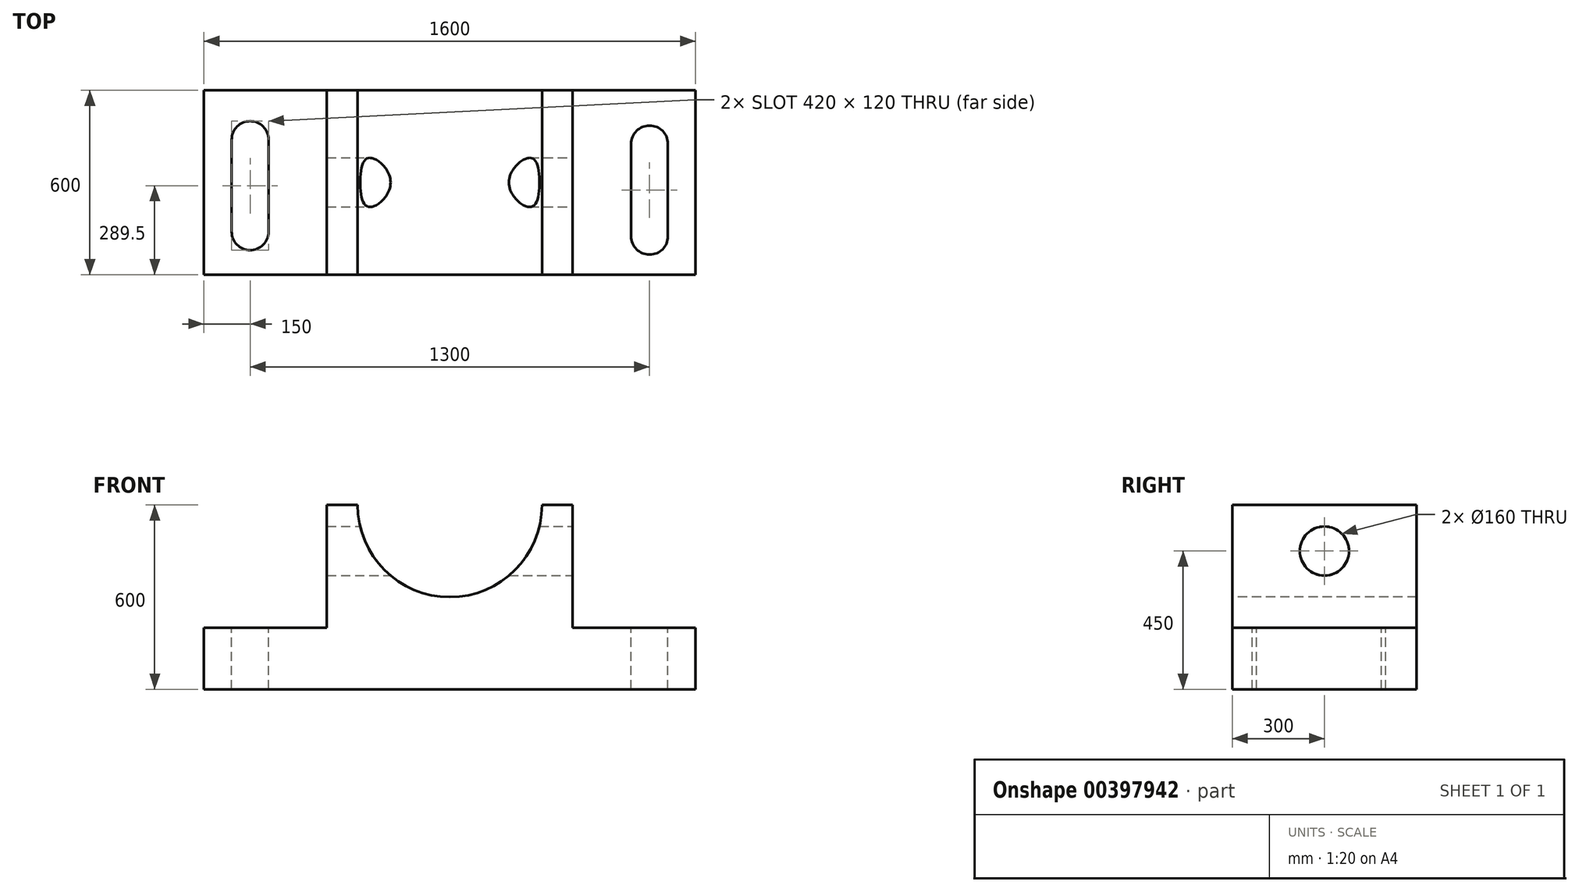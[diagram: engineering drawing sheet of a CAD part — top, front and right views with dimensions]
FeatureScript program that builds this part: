
annotation { "Feature Type Name" : "Feature", "Feature Type Description" : "" }
export const myFeature = defineFeature(function(context is Context, id is Id, definition is map)
    precondition{}
    {
        {
            var Q0;
            Q0=qCreatedBy(makeId("Front.planeOp"),FACE);
            var sketch = newSketch(context, id + "F0", { "sketchPlane" : qUnion([Q0])});
            skLineSegment(sketch, "E0.bottom", {"start": v(-800, -300) * mm, "end": v(800, -300) * mm});
            skLineSegment(sketch, "E0.top", {"start": v(-800, 300) * mm, "end": v(800, 300) * mm});
            skLineSegment(sketch, "E0.left", {"start": v(-800, -300) * mm, "end": v(-800, 300) * mm});
            skLineSegment(sketch, "E0.right", {"start": v(800, -300) * mm, "end": v(800, 300) * mm});
            skPoint(sketch, "E0.middle", {"position": v(0, 0) * mm});
            skLineSegment(sketch, "E1.bottom", {"start": v(-400, 300) * mm, "end": v(-800, 300) * mm});
            skLineSegment(sketch, "E1.top", {"start": v(-400, -100) * mm, "end": v(-800, -100) * mm});
            skLineSegment(sketch, "E1.left", {"start": v(-400, 300) * mm, "end": v(-400, -100) * mm});
            skLineSegment(sketch, "E1.right", {"start": v(-800, 300) * mm, "end": v(-800, -100) * mm});
            skLineSegment(sketch, "E2.bottom", {"start": v(400, 300) * mm, "end": v(800, 300) * mm});
            skLineSegment(sketch, "E2.top", {"start": v(400, -100) * mm, "end": v(800, -100) * mm});
            skLineSegment(sketch, "E2.left", {"start": v(400, 300) * mm, "end": v(400, -100) * mm});
            skLineSegment(sketch, "E2.right", {"start": v(800, 300) * mm, "end": v(800, -100) * mm});
            skSolve(sketch);
        }
        {
            var Q0;
            Q0=makeQuery(id+"F0.imprint","IMPRINT",FACE,{"disambiguationData":[TD([[makeQuery(id+"F0.imprint","IMPRINT",EDGE,{"derivedFrom":sQuery(id+"F0.wireOp",EDGE,"E0.bottom")}),1.0]])]});
            extrude(context, id + "F1", {"entities" : qUnion([Q0]), "depth" : 600 * mm});
        }
        {
            var Q0;
            Q0=makeQuery(id+"F1.opExtrude","CAP_FACE",FACE,{"disambiguationData":[OSD([sQuery(id+"F0.wireOp",EDGE,"E0.bottom"),sQuery(id+"F0.wireOp",EDGE,"E0.top"),sQuery(id+"F0.wireOp",EDGE,"E0.left"),sQuery(id+"F0.wireOp",EDGE,"E0.right"),sQuery(id+"F0.wireOp",EDGE,"E1.top"),sQuery(id+"F0.wireOp",EDGE,"E1.left"),sQuery(id+"F0.wireOp",EDGE,"E2.top"),sQuery(id+"F0.wireOp",EDGE,"E2.left")])],"isStart":false});
            var sketch = newSketch(context, id + "F2", { "sketchPlane" : qUnion([Q0])});
            skArc(sketch, "E3", {"start": v(-300, 300) * mm, "mid": v(0, 0) * mm, "end": v(300, 300) * mm});
            skSolve(sketch);
        }
        {
            var Q0;
            Q0 = qSketchRegion(id + "F2", true);
            var Q1;
            {var subQ0=sQuery(id+"F2.wireOp",EDGE,"E3");Q1=makeQuery(id+"F2.imprint","IMPRINT",FACE,{"disambiguationData":[TD([[makeQuery(id+"F2.imprint","IMPRINT",EDGE,{"derivedFrom":subQ0}),1.0]])]});}
            extrude(context, id + "F3", {"entities" : qUnion([Q0, Q1]), "operationType" : NewBodyOperationType.REMOVE, "endBound" : BoundingType.THROUGH_ALL, "oppositeDirection" : true, "depth" : 25 * mm});
        }
        {
            var Q0;
            Q0=makeQuery(id+"F1.opExtrude","SWEPT_FACE",FACE,{"disambiguationData":[OSD([sQuery(id+"F0.wireOp",EDGE,"E0.right")])]});
            var sketch = newSketch(context, id + "F4", { "sketchPlane" : qUnion([Q0])});
            skCircle(sketch, "E4", {"center": v(-300, 150) * mm, "radius": 80 * mm});
            skPoint(sketch, "E4.centerSnap0", {"position": v(-300, -100) * mm});
            skSolve(sketch);
        }
        {
            var Q0;
            Q0=makeQuery(id+"F4.imprint","IMPRINT",FACE,{"disambiguationData":[TD([[makeQuery(id+"F4.imprint","IMPRINT",EDGE,{"derivedFrom":sQuery(id+"F4.wireOp",EDGE,"E4")}),1.0]])]});
            extrude(context, id + "F5", {"entities" : qUnion([Q0]), "operationType" : NewBodyOperationType.REMOVE, "endBound" : BoundingType.THROUGH_ALL, "oppositeDirection" : true, "depth" : 25 * mm});
        }
        {
            var Q0;
            Q0=makeQuery(id+"F1.opExtrude","SWEPT_FACE",FACE,{"disambiguationData":[OSD([sQuery(id+"F0.wireOp",EDGE,"E2.top")])]});
            var sketch = newSketch(context, id + "F6", { "sketchPlane" : qUnion([Q0])});
            skLineSegment(sketch, "E5.left", {"start": v(590, -474.9) * mm, "end": v(590, -174.9) * mm});
            skLineSegment(sketch, "E5.right", {"start": v(710, -474.9) * mm, "end": v(710, -174.9) * mm});
            skPoint(sketch, "E5.middle", {"position": v(650, -324.9) * mm});
            skArc(sketch, "E6", {"start": v(710, -174.9) * mm, "mid": v(650, -114.9) * mm, "end": v(590, -174.9) * mm});
            skArc(sketch, "E7", {"start": v(590, -474.9) * mm, "mid": v(650, -534.9) * mm, "end": v(710, -474.9) * mm});
            skLineSegment(sketch, "E8.left", {"start": v(-710, -460.5) * mm, "end": v(-710, -160.5) * mm});
            skLineSegment(sketch, "E8.right", {"start": v(-590, -460.5) * mm, "end": v(-590, -160.5) * mm});
            skPoint(sketch, "E8.middle", {"position": v(-650, -310.5) * mm});
            skArc(sketch, "E9", {"start": v(-590, -160.5) * mm, "mid": v(-650, -100.5) * mm, "end": v(-710, -160.5) * mm});
            skArc(sketch, "E10", {"start": v(-710, -460.5) * mm, "mid": v(-650, -520.5) * mm, "end": v(-590, -460.5) * mm});
            skSolve(sketch);
        }
        {
            var Q0;
            Q0=makeQuery(id+"F6.imprint","IMPRINT",FACE,{"disambiguationData":[TD([[makeQuery(id+"F6.imprint","IMPRINT",EDGE,{"derivedFrom":sQuery(id+"F6.wireOp",EDGE,"E5.left")}),-1.0]])]});
            var Q1;
            Q1=makeQuery(id+"F6.imprint","IMPRINT",FACE,{"disambiguationData":[TD([[makeQuery(id+"F6.imprint","IMPRINT",EDGE,{"derivedFrom":sQuery(id+"F6.wireOp",EDGE,"E8.left")}),-1.0]])]});
            extrude(context, id + "F7", {"entities" : qUnion([Q0, Q1]), "operationType" : NewBodyOperationType.REMOVE, "endBound" : BoundingType.THROUGH_ALL, "oppositeDirection" : true, "depth" : 25 * mm});
        }
    });
